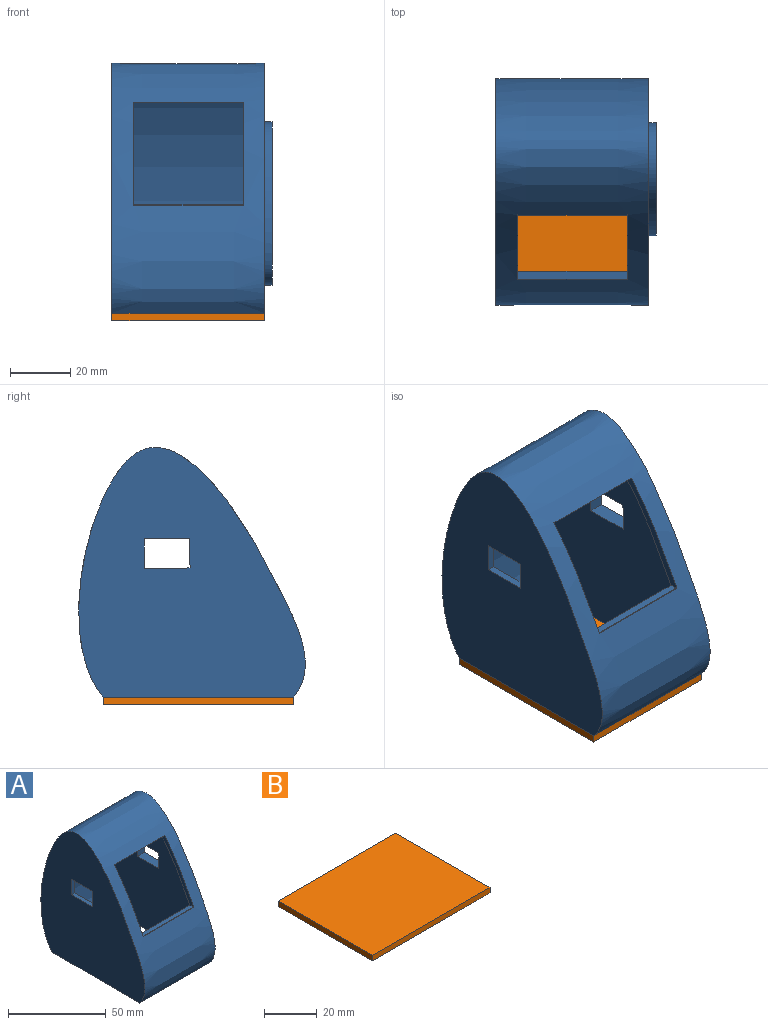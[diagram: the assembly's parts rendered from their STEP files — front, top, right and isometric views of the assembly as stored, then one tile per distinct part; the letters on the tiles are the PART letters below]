
ASSEMBLY  parts=2 mates=1
PART A: 22 faces, bbox 53.3x82.9x91 mm
  f0: extruded ~80.85x70.31mm, area 7249.9mm2, adj f1,f5,f6,f7,f8,f9,f10
  f1: plane 63.37x50.8mm, normal (0,0.01,-1), area 646.5mm2, adj f0,f2,f3,f4,f5,f6
  f2: extruded ~83.4x75.22mm, area 8599.6mm2, adj f1,f3,f4,f7,f9,f10,f11
  f3: plane 91.02x82.95mm, normal (1,0,0), area 3097.6mm2, adj f1,f2,f20
  f4: plane 91.02x82.95mm, normal (-1,0,0), area 4530.3mm2, adj f1,f2,f12,f13,f14,f15
  f5: plane 80.92x70.33mm, normal (-1,0,0), area 4033.5mm2, adj f0,f1,f16,f17,f18,f19
  f6: plane 80.92x70.33mm, normal (1,0,0), area 4033.5mm2, adj f0,f1,f12,f13,f14,f15
  f7: plane 34.93x24.78mm, normal (1,0,0), area 103.6mm2, adj f0,f2,f8,f10,f11
  f8: plane 36.57x2.7mm, normal (0,0,1), area 98.9mm2, adj f0,f7,f9,f11
  f9: plane 34.93x24.78mm, normal (-1,0,0), area 103.6mm2, adj f0,f2,f8,f10,f11
  f10: plane 36.57x3.39mm, normal (0,0,-1), area 123.9mm2, adj f0,f2,f7,f9
  f11: plane 36.57x0.29mm, normal (0,1,0), area 10.6mm2, adj f2,f7,f8,f9
  f12: plane 15.24x2.54mm, normal (0,0,-1), area 38.7mm2, adj f4,f6,f13,f15
  f13: plane 9.79x2.54mm, normal (0,-1,0), area 24.9mm2, adj f4,f6,f12,f14
  f14: plane 15.24x2.54mm, normal (0,0,1), area 38.7mm2, adj f4,f6,f13,f15
  f15: plane 9.79x2.54mm, normal (0,1,0), area 24.9mm2, adj f4,f6,f12,f14
  f16: plane 9.79x5.08mm, normal (0,1,0), area 49.7mm2, adj f5,f17,f19,f21
  f17: plane 15.24x5.08mm, normal (0,0,1), area 77.4mm2, adj f5,f16,f18,f21
  f18: plane 9.79x5.08mm, normal (0,-1,0), area 49.7mm2, adj f5,f17,f19,f21
  f19: plane 15.24x5.08mm, normal (0,0,-1), area 77.4mm2, adj f5,f16,f18,f21
  f20: extruded ~54.36x37.38mm, area 377.5mm2, adj f3,f21
  f21: plane 59.65x42.39mm, normal (1,0,0), area 1432.6mm2, adj f16,f17,f18,f19,f20
PART B: 6 faces, bbox 63.4x50.8x2.5 mm
  f0: plane 50.8x2.54mm, normal (-1,0,0), area 129mm2, adj f1,f3,f4,f5
  f1: plane 63.37x2.54mm, normal (0,-1,0), area 161mm2, adj f0,f2,f4,f5
  f2: plane 50.8x2.54mm, normal (1,0,0), area 129mm2, adj f1,f3,f4,f5
  f3: plane 63.37x2.54mm, normal (0,1,0), area 161mm2, adj f0,f2,f4,f5
  f4: plane 63.37x50.8mm, normal (0,0,1), area 3219.3mm2, adj f0,f1,f2,f3
  f5: plane 63.37x50.8mm, normal (0,0,-1), area 3219.3mm2, adj f0,f1,f2,f3
PLACE A rot(axis=(-1,0,0),0.4deg) t=(-45.93,-7.73,-1.49)mm
PLACE B rot(axis=(0,0,-1),90deg) t=(-20.53,-6.08,-32.75)mm
MATE fastened A.f1 <-> B.f4  axis (0,0,-1) through (4.87,-37.76,-30.21)mm
